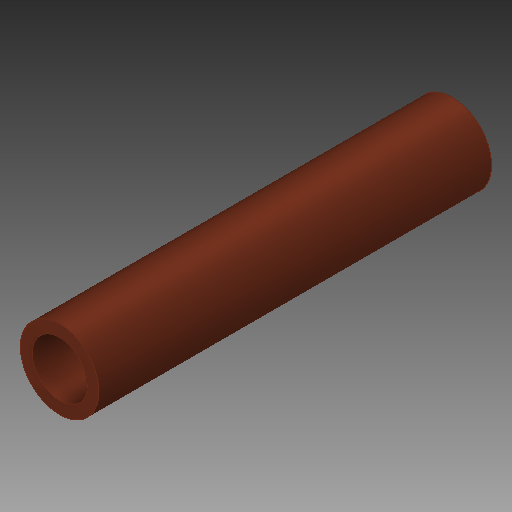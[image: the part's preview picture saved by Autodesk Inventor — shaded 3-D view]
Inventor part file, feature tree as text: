
AUTODESK INVENTOR PART (.ipt)
format: ipt  version: 2019 (Build 230136000, 136)  size: 100,352 bytes
history: native  units: mm
features: extrude x2, sketch x2
ambient origin geometry x8: Origin, YZ Plane, XZ Plane, XY Plane, X Axis, Y Axis, Z Axis, Center Point
bodies: Solid1 (feature_tree)
feature tree (4):
  extrude  "Extrusion1"  Depth=500.0mm TaperAngle=0.0deg
  extrude  "Extrusion2"  Depth=500.0mm TaperAngle=0.0deg
  sketch  "Sketch1"  dims[d0=100.0mm d1=500.0mm d2=0.0mm]
  sketch  "Sketch2"  dims[d3=70.0mm d4=500.0mm d5=0.0mm]
